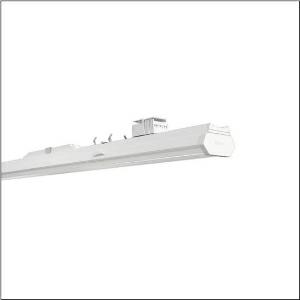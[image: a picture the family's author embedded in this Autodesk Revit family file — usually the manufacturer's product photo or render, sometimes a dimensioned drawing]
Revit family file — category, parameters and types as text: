
# Revit family: licross_r__11_protected_mo_51tp12cn58xf_fcc9
name_source: partatom
category: Lighting Fixtures
units: mm (PartAtom-declared; Revit-internal decimal feet)

## family parameters
Cut with Voids When Loaded = No
Host = Face
Light Source = No
Part Type = Normal
Room Calculation Point = No
Round Connector Dimension = Use Diameter
Shared = No

## types (1)
- --- (1 x LED, 8190 lm, 49 W, 5000K)
    Apparent Load = 49 VA
    CIE Flux Codes = 73 92 98 99 100
    Color Rendering = 80
    Color Temperature = 5000K
    Default Elevation = 1800 mm
    Description = Licross® 11 Protected MOluminaire insert, length: 1.500mm, width: 90mm, height: 101mm, LED rated luminous flux: 8.190lm, light colour: 850, control gear: ON/OFF Multilumen, CLOi, control gear: ECG Multilumen, with plug, 3-pole, with phase selection, mains connection: 220..240V, AC, 50/60Hz, halogen-free wiring, primary optical cover: cover, of PMMA, light emission: direct with ceiling illumination distribution, protection rating (complete): IP64, insulation class (complete): insulation class I (protective earthing), certification: CE, ENEC, VDE, protection symbol: D if used in an environment with conductive dust loads with corresponding accessories, permissible ambient temperature for indoor applications: -35..+40°C, reducing of maximum allowable ambient temperature of 5°C with ceiling mounting, corresponds to IFS (International Featured Standards) requirements for safety and quality in the food industry, packaging unit: 1 piece
    Height = 92 mm
    Lamp = 1 x LED
    Lamp Light Flux = 8190 lm
    Lamp Power = 49 W
    Lamp count = 1
    Length = 1500 mm
    Luminous efficacy = 167 lm/W
    Manufacturer = Siteco
    ModVariant = No
    Model = 51TP12CN58XF
    Mounting Place = Ceiling
    Mounting Type = Pendant
    Number of Poles = 1
    OnlyDefault = Yes
    Power Factor = 1
    Product Name = Licross® 11 Protected MO
    Product group = luminaire insert
    ProductGroupID = 902
    Protection Class = Protection class I
    Protection Degree = IP 64
    RLX_Detail_Level = 1
    RlxData = <blob elided: 21741 chars, md5=63c5adfb>
    Socket = socket
    Standby Power = 0 W
    System Light Flux = 8190 lm
    System Power = 49 W
    Type Comments = factory setting: luminous flux: 100 % | (A | C | E) | 111 mA
    Type Image = l_1256148.jpg
    URL = http://relux.com
    VarID = @adj_137281
    Voltage = 0 V
    Weight = 0.00 kg
    Width = 88 mm

## geometry (parser evidence)
native form markers: Blend x4, Sweep x12
no freeform markers — native parametric forms only
